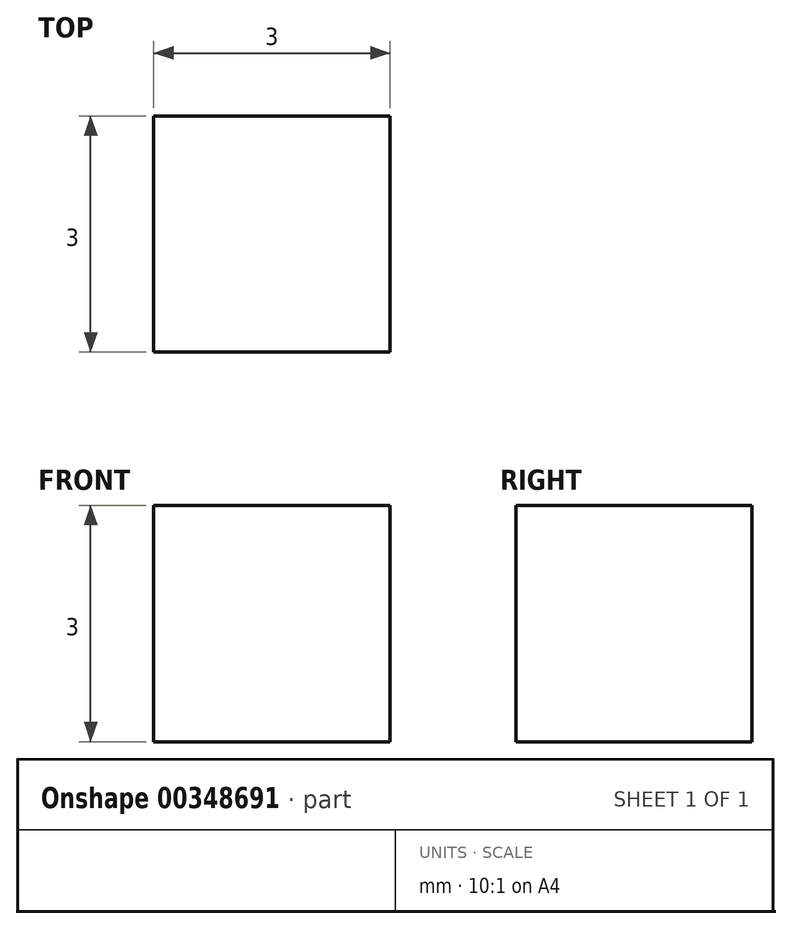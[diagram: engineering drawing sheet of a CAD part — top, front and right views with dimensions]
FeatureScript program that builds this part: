
annotation { "Feature Type Name" : "Feature", "Feature Type Description" : "" }
export const myFeature = defineFeature(function(context is Context, id is Id, definition is map)
    precondition{}
    {
        {
            var Q0;
            Q0=qCreatedBy(makeId("Front.planeOp"),FACE);
            var sketch = newSketch(context, id + "F0", { "sketchPlane" : qUnion([Q0])});
            skLineSegment(sketch, "E0.bottom", {"start": v(1.5, 1.5) * mm, "end": v(-1.5, 1.5) * mm});
            skLineSegment(sketch, "E0.top", {"start": v(1.5, -1.5) * mm, "end": v(-1.5, -1.5) * mm});
            skLineSegment(sketch, "E0.left", {"start": v(1.5, 1.5) * mm, "end": v(1.5, -1.5) * mm});
            skLineSegment(sketch, "E0.right", {"start": v(-1.5, 1.5) * mm, "end": v(-1.5, -1.5) * mm});
            skPoint(sketch, "E0.middle", {"position": v(0, 0) * mm});
            skSolve(sketch);
        }
        {
            var Q0;
            Q0 = qSketchRegion(id + "F0", true);
            extrude(context, id + "F1", {"entities" : qUnion([Q0]), "depth" : 3 * mm});
        }
    });
